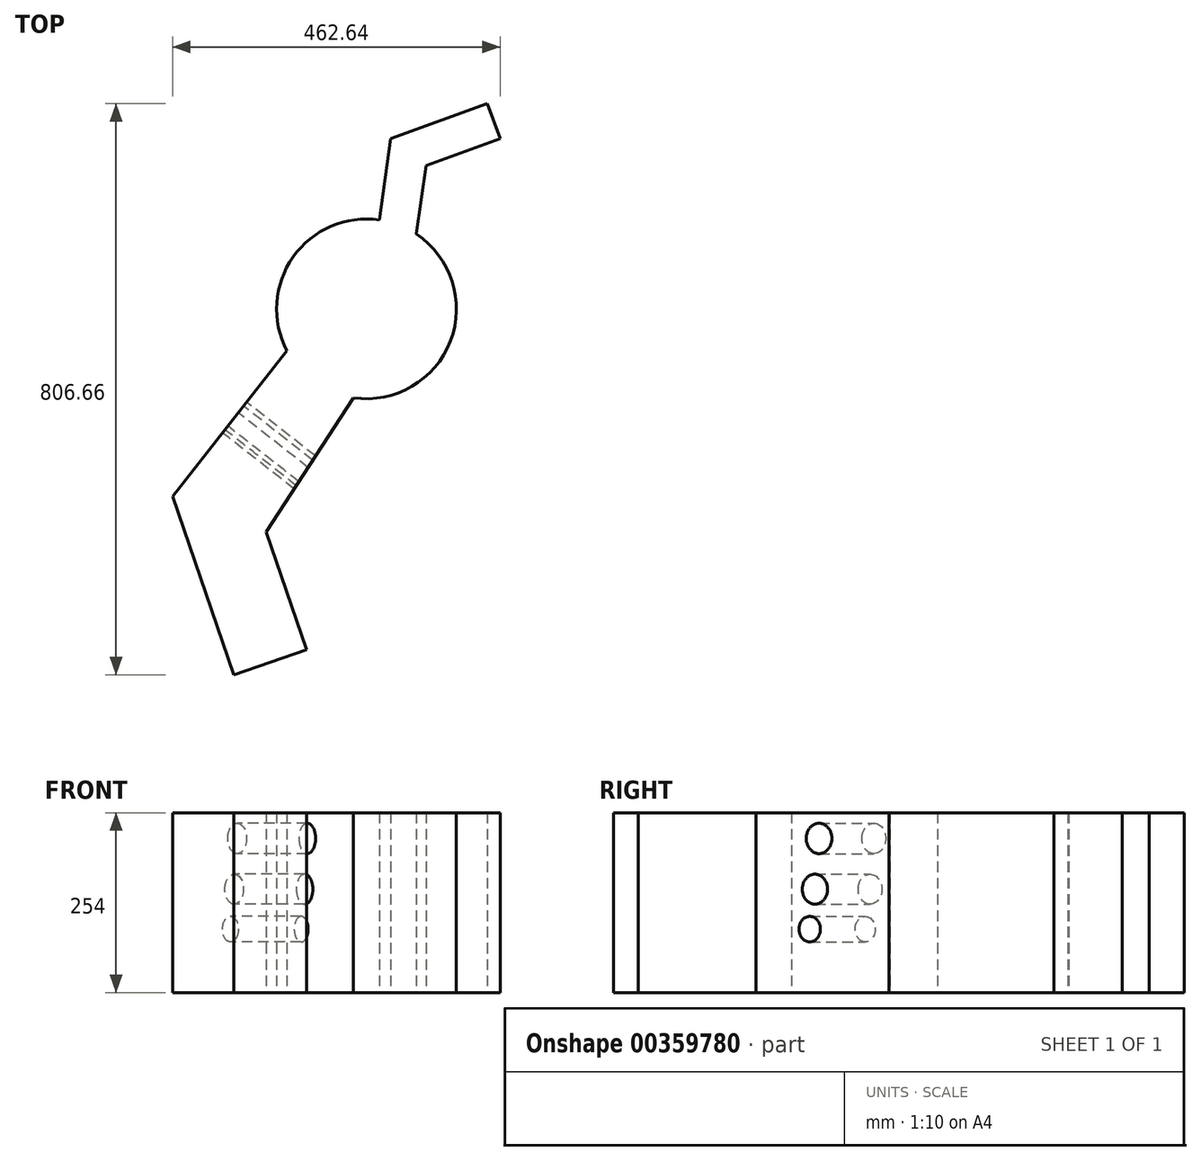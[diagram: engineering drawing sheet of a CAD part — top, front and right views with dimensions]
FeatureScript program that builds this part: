
annotation { "Feature Type Name" : "Feature", "Feature Type Description" : "" }
export const myFeature = defineFeature(function(context is Context, id is Id, definition is map)
    precondition{}
    {
        {
            var Q0;
            Q0=qCreatedBy(makeId("Top.planeOp"),FACE);
            var sketch = newSketch(context, id + "F0", { "sketchPlane" : qUnion([Q0])});
            skCircle(sketch, "E0", {"center": v(0, 0) * mm, "radius": 127 * mm});
            skLineSegment(sketch, "E1", {"start": v(0, 0) * mm, "end": v(34.34, 240.28) * mm});
            skLineSegment(sketch, "E2", {"start": v(34.34, 240.28) * mm, "end": v(170.76, 289.89) * mm});
            skLineSegment(sketch, "E3", {"start": v(170.76, 289.89) * mm, "end": v(188.8, 240.28) * mm});
            skLineSegment(sketch, "E4", {"start": v(188.8, 240.28) * mm, "end": v(84.14, 202.22) * mm});
            skLineSegment(sketch, "E5", {"start": v(84.14, 202.22) * mm, "end": v(52.97, -15.91) * mm});
            skLineSegment(sketch, "E6", {"start": v(52.97, -15.91) * mm, "end": v(-141.77, -315.32) * mm});
            skLineSegment(sketch, "E7", {"start": v(-141.77, -315.32) * mm, "end": v(-84.72, -481.5) * mm});
            skLineSegment(sketch, "E8", {"start": v(-84.72, -481.5) * mm, "end": v(-187.43, -516.77) * mm});
            skLineSegment(sketch, "E9", {"start": v(-187.43, -516.77) * mm, "end": v(-273.84, -265.07) * mm});
            skLineSegment(sketch, "E10", {"start": v(-273.84, -265.07) * mm, "end": v(-54.95, 14.57) * mm});
            skSolve(sketch);
        }
        {
            var Q0;
            {var subQ5=sQuery(id+"F0.wireOp",EDGE,"E7");Q0=makeQuery(id+"F0.imprint","IMPRINT",FACE,{"disambiguationData":[TD([[makeQuery(id+"F0.imprint","IMPRINT",EDGE,{"derivedFrom":subQ5}),-1.0]])]});}
            var Q1;
            {var subQ0=sQuery(id+"F0.wireOp",EDGE,"E5");var subQ1=sQuery(id+"F0.wireOp",EDGE,"E0");var subQ2=makeQuery(id+"F0.imprint","INTERSECT",VERTEX,{"derivedFrom":[subQ1,subQ0]});Q1=makeQuery(id+"F0.imprint","IMPRINT",FACE,{"disambiguationData":[TD([[makeQuery(id+"F0.imprint","IMPRINT",EDGE,{"disambiguationData":[TD([[subQ2,1.0]])],"derivedFrom":subQ1}),1.0]])]});}
            var Q2;
            {var subQ0=sQuery(id+"F0.wireOp",EDGE,"E2");Q2=makeQuery(id+"F0.imprint","IMPRINT",FACE,{"disambiguationData":[TD([[makeQuery(id+"F0.imprint","IMPRINT",EDGE,{"derivedFrom":subQ0}),-1.0]])]});}
            var Q3;
            {var subQ3=sQuery(id+"F0.wireOp",EDGE,"E0");var subQ7=makeQuery(id+"F0.imprint","INTERSECT",VERTEX,{"derivedFrom":[subQ3,sQuery(id+"F0.wireOp",EDGE,"E1")]});Q3=makeQuery(id+"F0.imprint","IMPRINT",FACE,{"disambiguationData":[TD([[makeQuery(id+"F0.imprint","IMPRINT",EDGE,{"disambiguationData":[TD([[subQ7,1.0]])],"derivedFrom":subQ3}),1.0]])]});}
            extrude(context, id + "F1", {"entities" : qUnion([Q0, Q1, Q2, Q3]), "depth" : 254 * mm});
        }
        {
            var Q0;
            Q0=makeQuery(id+"F1.opExtrude","SWEPT_FACE",FACE,{"disambiguationData":[OSD([sQuery(id+"F0.wireOp",EDGE,"E10")])]});
            var sketch = newSketch(context, id + "F2", { "sketchPlane" : qUnion([Q0])});
            skCircle(sketch, "E11", {"center": v(229.63, 217.7) * mm, "radius": 21.5 * mm});
            skCircle(sketch, "E12", {"center": v(236.5, 145.95) * mm, "radius": 21.24 * mm});
            skCircle(sketch, "E13", {"center": v(245.3, 89.51) * mm, "radius": 18.04 * mm});
            skSolve(sketch);
        }
        {
            var Q0;
            Q0=makeQuery(id+"F2.imprint","IMPRINT",FACE,{"disambiguationData":[TD([[makeQuery(id+"F2.imprint","IMPRINT",EDGE,{"derivedFrom":sQuery(id+"F2.wireOp",EDGE,"E11")}),1.0]])]});
            var Q1;
            Q1=makeQuery(id+"F2.imprint","IMPRINT",FACE,{"disambiguationData":[TD([[makeQuery(id+"F2.imprint","IMPRINT",EDGE,{"derivedFrom":sQuery(id+"F2.wireOp",EDGE,"E12")}),1.0]])]});
            var Q2;
            Q2=makeQuery(id+"F2.imprint","IMPRINT",FACE,{"disambiguationData":[TD([[makeQuery(id+"F2.imprint","IMPRINT",EDGE,{"derivedFrom":sQuery(id+"F2.wireOp",EDGE,"E13")}),1.0]])]});
            extrude(context, id + "F3", {"entities" : qUnion([Q0, Q1, Q2]), "operationType" : NewBodyOperationType.REMOVE, "oppositeDirection" : true, "depth" : 508 * mm});
        }
    });
